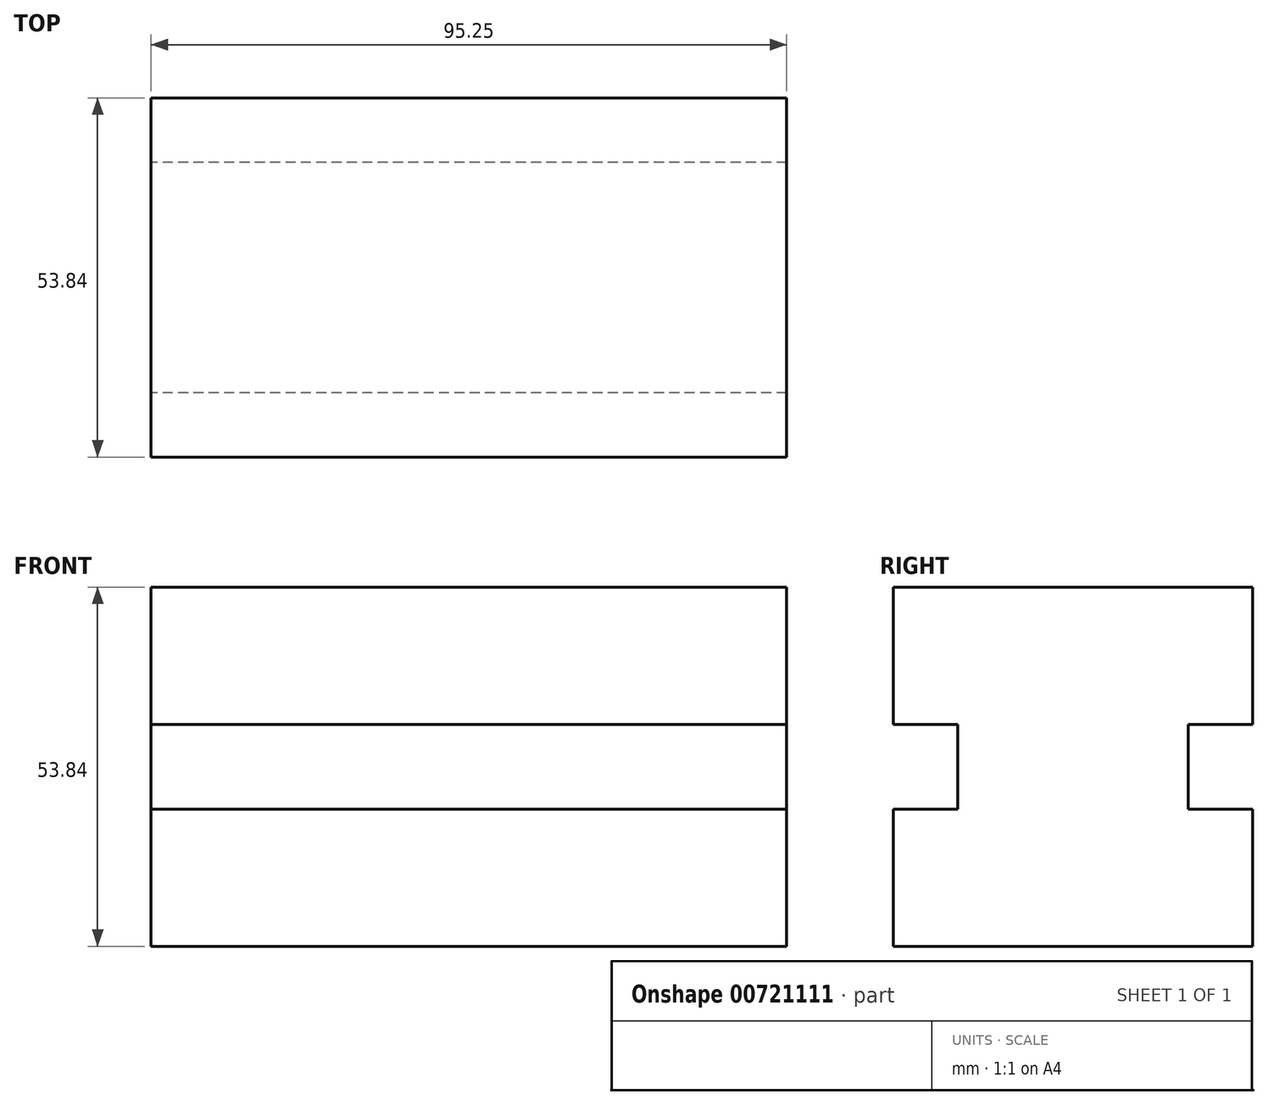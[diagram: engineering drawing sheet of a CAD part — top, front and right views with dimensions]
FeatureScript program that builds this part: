
annotation { "Feature Type Name" : "Feature", "Feature Type Description" : "" }
export const myFeature = defineFeature(function(context is Context, id is Id, definition is map)
    precondition{}
    {
        {
            var Q0;
            Q0=qCreatedBy(makeId("Right.planeOp"),FACE);
            var sketch = newSketch(context, id + "F0", { "sketchPlane" : qUnion([Q0])});
            skLineSegment(sketch, "E0.bottom", {"start": v(26.92, -26.92) * mm, "end": v(-26.92, -26.92) * mm});
            skLineSegment(sketch, "E0.top", {"start": v(26.92, 26.92) * mm, "end": v(-26.92, 26.92) * mm});
            skLineSegment(sketch, "E0.left", {"start": v(26.92, -26.92) * mm, "end": v(26.92, -6.35) * mm});
            skLineSegment(sketch, "E0.right", {"start": v(-26.92, -26.92) * mm, "end": v(-26.92, -6.35) * mm});
            skPoint(sketch, "E0.middle", {"position": v(0, 0) * mm});
            skLineSegment(sketch, "E1.bottom", {"start": v(-26.92, 6.35) * mm, "end": v(-17.27, 6.35) * mm});
            skLineSegment(sketch, "E1.top", {"start": v(-26.92, -6.35) * mm, "end": v(-17.27, -6.35) * mm});
            skLineSegment(sketch, "E1.right", {"start": v(-17.27, 6.35) * mm, "end": v(-17.27, -6.35) * mm});
            skLineSegment(sketch, "E2", {"start": v(0, 32.65) * mm, "end": v(0, -39.88) * mm, "construction": true});
            skLineSegment(sketch, "E3.MirrorCS", {"start": v(26.92, 6.35) * mm, "end": v(17.27, 6.35) * mm});
            skLineSegment(sketch, "E4.MirrorCS", {"start": v(17.27, 6.35) * mm, "end": v(17.27, -6.35) * mm});
            skLineSegment(sketch, "E5.MirrorCS", {"start": v(26.92, -6.35) * mm, "end": v(17.27, -6.35) * mm});
            skLineSegment(sketch, "E6.trimOffspring", {"start": v(-26.92, 6.35) * mm, "end": v(-26.92, 26.92) * mm});
            skLineSegment(sketch, "E7.trimOffspring", {"start": v(26.92, 6.35) * mm, "end": v(26.92, 26.92) * mm});
            skSolve(sketch);
        }
        {
            var Q0;
            Q0=makeQuery(id+"F0.imprint","IMPRINT",FACE,{"disambiguationData":[TD([[makeQuery(id+"F0.imprint","IMPRINT",EDGE,{"derivedFrom":sQuery(id+"F0.wireOp",EDGE,"E0.bottom")}),-1.0]])]});
            extrude(context, id + "F1", {"entities" : qUnion([Q0]), "depth" : 95.25 * mm, "offsetDistance" : 25.4 * mm});
        }
    });
